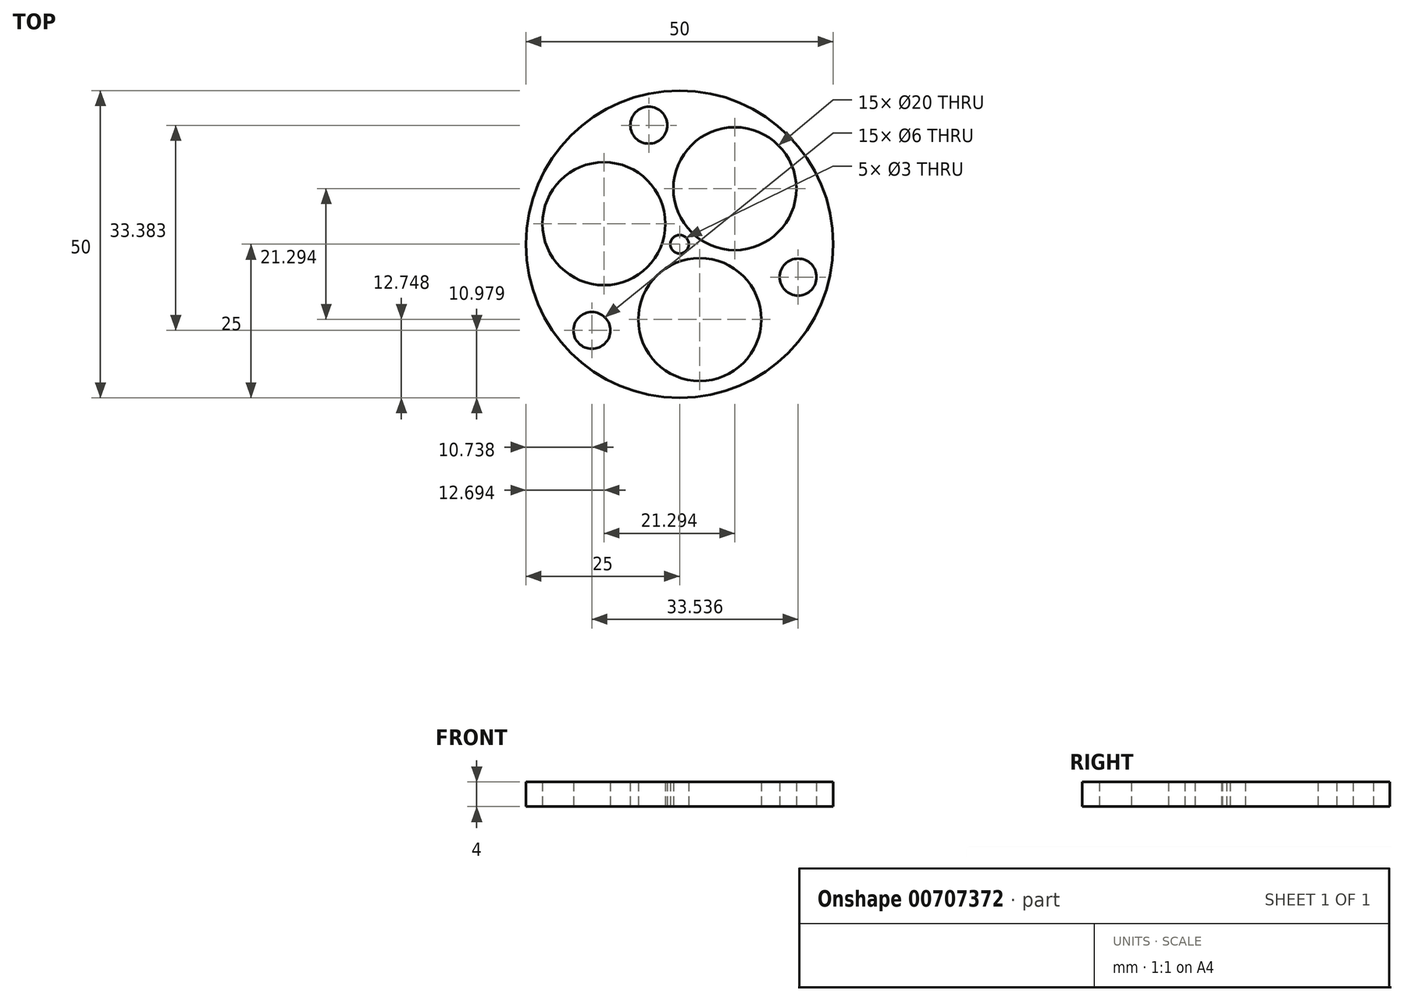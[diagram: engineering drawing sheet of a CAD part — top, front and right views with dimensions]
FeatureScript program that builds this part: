
annotation { "Feature Type Name" : "Feature", "Feature Type Description" : "" }
export const myFeature = defineFeature(function(context is Context, id is Id, definition is map)
    precondition{}
    {
        {
            var Q0;
            Q0=qCreatedBy(makeId("Top.planeOp"),FACE);
            var sketch = newSketch(context, id + "F0", { "sketchPlane" : qUnion([Q0])});
            skCircle(sketch, "E0", {"center": v(0, 0) * mm, "radius": 25 * mm});
            skCircle(sketch, "E1", {"center": v(8.99, 9.04) * mm, "radius": 10 * mm});
            skCircle(sketch, "E2.1.0", {"center": v(-12.3, 3.34) * mm, "radius": 10 * mm});
            skCircle(sketch, "E2.2.0", {"center": v(3.28, -12.25) * mm, "radius": 10 * mm});
            skPoint(sketch, "E2.center", {"position": v(-0.01, 0.04) * mm});
            skCircle(sketch, "E3", {"center": v(0, 0) * mm, "radius": 12.75 * mm, "construction": true});
            skLineSegment(sketch, "E4", {"start": v(-0.01, 0.04) * mm, "end": v(8.99, 9.04) * mm, "construction": true});
            skLineSegment(sketch, "E5", {"start": v(-0.01, 0.04) * mm, "end": v(3.28, -12.25) * mm, "construction": true});
            skLineSegment(sketch, "E6", {"start": v(-0.01, 0.04) * mm, "end": v(-12.3, 3.34) * mm, "construction": true});
            skCircle(sketch, "E7", {"center": v(0, 0) * mm, "radius": 20 * mm, "construction": true});
            skCircle(sketch, "E8", {"center": v(-5.01, 19.36) * mm, "radius": 3 * mm});
            skCircle(sketch, "E9.1.0", {"center": v(-14.26, -14.02) * mm, "radius": 3 * mm});
            skCircle(sketch, "E9.2.0", {"center": v(19.27, -5.34) * mm, "radius": 3 * mm});
            skCircle(sketch, "E10", {"center": v(0, 0) * mm, "radius": 1.5 * mm});
            skSolve(sketch);
        }
        {
            var Q0;
            Q0=makeQuery(id+"F0.imprint","IMPRINT",FACE,{"disambiguationData":[TD([[makeQuery(id+"F0.imprint","IMPRINT",EDGE,{"derivedFrom":sQuery(id+"F0.wireOp",EDGE,"E0")}),1.0]])]});
            extrude(context, id + "F1", {"entities" : qUnion([Q0]), "depth" : 4 * mm, "offsetDistance" : 25 * mm});
        }
    });
